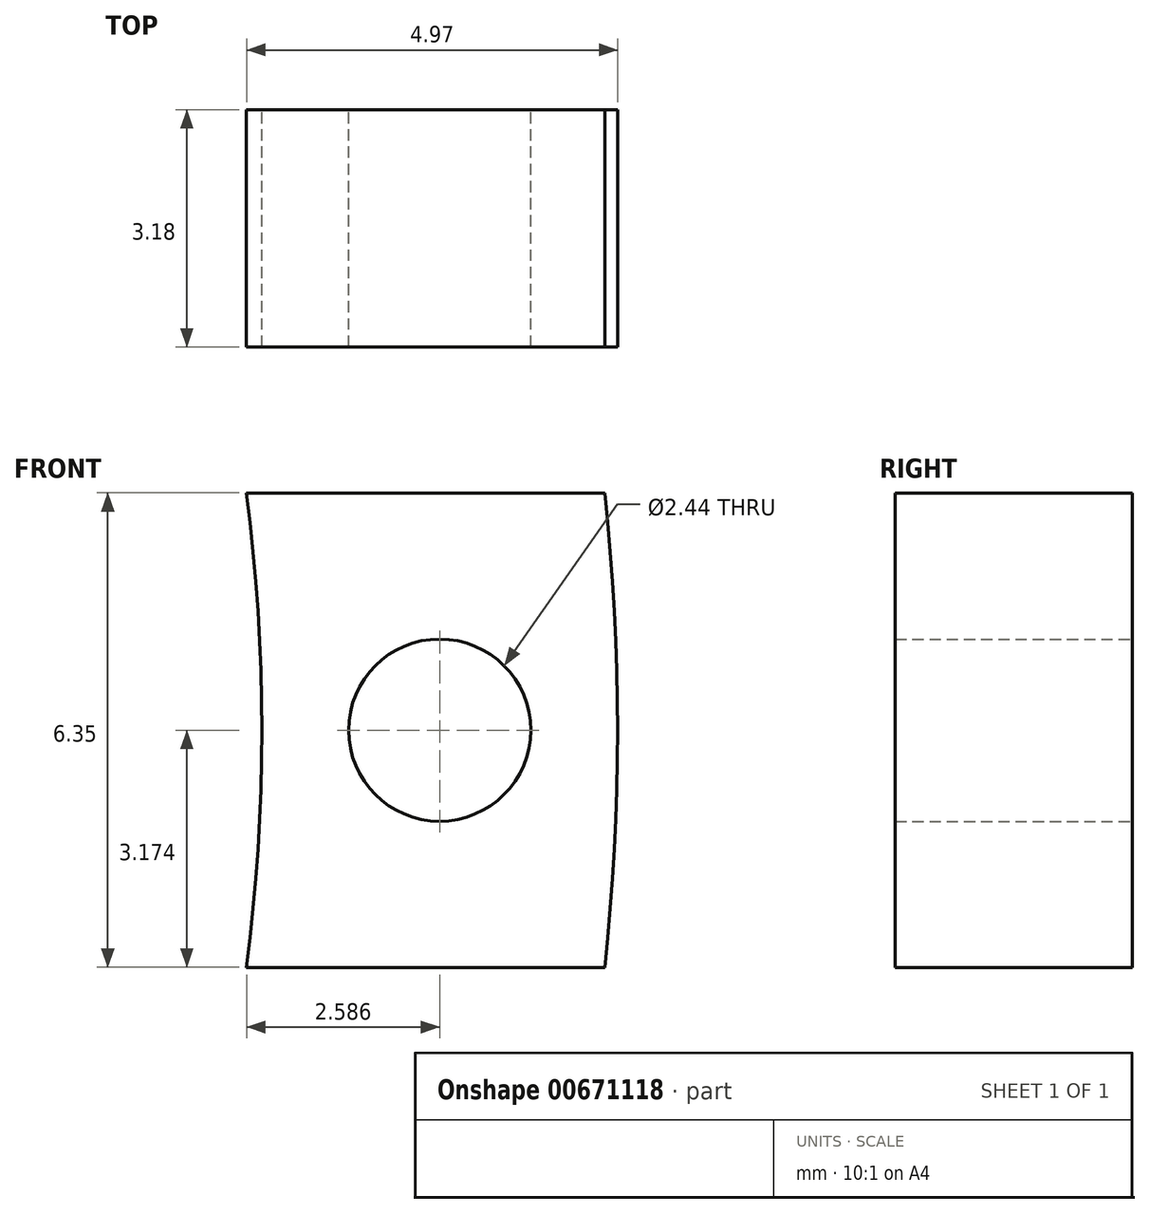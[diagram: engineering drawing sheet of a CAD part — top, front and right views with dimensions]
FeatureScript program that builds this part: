
annotation { "Feature Type Name" : "Feature", "Feature Type Description" : "" }
export const myFeature = defineFeature(function(context is Context, id is Id, definition is map)
    precondition{}
    {
        {
            var Q0;
            Q0=qCreatedBy(makeId("Front.planeOp"),FACE);
            var sketch = newSketch(context, id + "F0", { "sketchPlane" : qUnion([Q0])});
            skCircle(sketch, "E0", {"center": v(25.29, 24.66) * mm, "radius": 24.6 * mm});
            skCircle(sketch, "E1", {"center": v(25.29, 24.66) * mm, "radius": 29.37 * mm});
            skCircle(sketch, "E2", {"center": v(25.29, 24.66) * mm, "radius": 26.99 * mm});
            skLineSegment(sketch, "E3", {"start": v(25.29, 24.66) * mm, "end": v(62.05, 24.66) * mm, "construction": true});
            skLineSegment(sketch, "E4", {"start": v(49.69, 27.84) * mm, "end": v(54.48, 27.84) * mm});
            skLineSegment(sketch, "E5", {"start": v(49.69, 21.49) * mm, "end": v(54.48, 21.49) * mm});
            skCircle(sketch, "E6", {"center": v(52.28, 24.66) * mm, "radius": 1.22 * mm});
            skSolve(sketch);
        }
        {
            var Q0;
            {var subQ0=sQuery(id+"F0.wireOp",EDGE,"E4");var subQ1=sQuery(id+"F0.wireOp",EDGE,"E1");var subQ2=makeQuery(id+"F0.imprint","INTERSECT",VERTEX,{"derivedFrom":[subQ1,subQ0]});Q0=makeQuery(id+"F0.imprint","IMPRINT",FACE,{"disambiguationData":[TD([[makeQuery(id+"F0.imprint","IMPRINT",EDGE,{"disambiguationData":[TD([[subQ2,1.0]])],"derivedFrom":subQ1}),1.0]])]});}
            var Q1;
            {var subQ0=sQuery(id+"F0.wireOp",EDGE,"E4");var subQ1=sQuery(id+"F0.wireOp",EDGE,"E0");var subQ2=makeQuery(id+"F0.imprint","INTERSECT",VERTEX,{"derivedFrom":[subQ1,subQ0]});Q1=makeQuery(id+"F0.imprint","IMPRINT",FACE,{"disambiguationData":[TD([[makeQuery(id+"F0.imprint","IMPRINT",EDGE,{"disambiguationData":[TD([[subQ2,1.0]])],"derivedFrom":subQ1}),-1.0]])]});}
            extrude(context, id + "F1", {"entities" : qUnion([Q0, Q1]), "depth" : 3.17 * mm});
        }
    });
